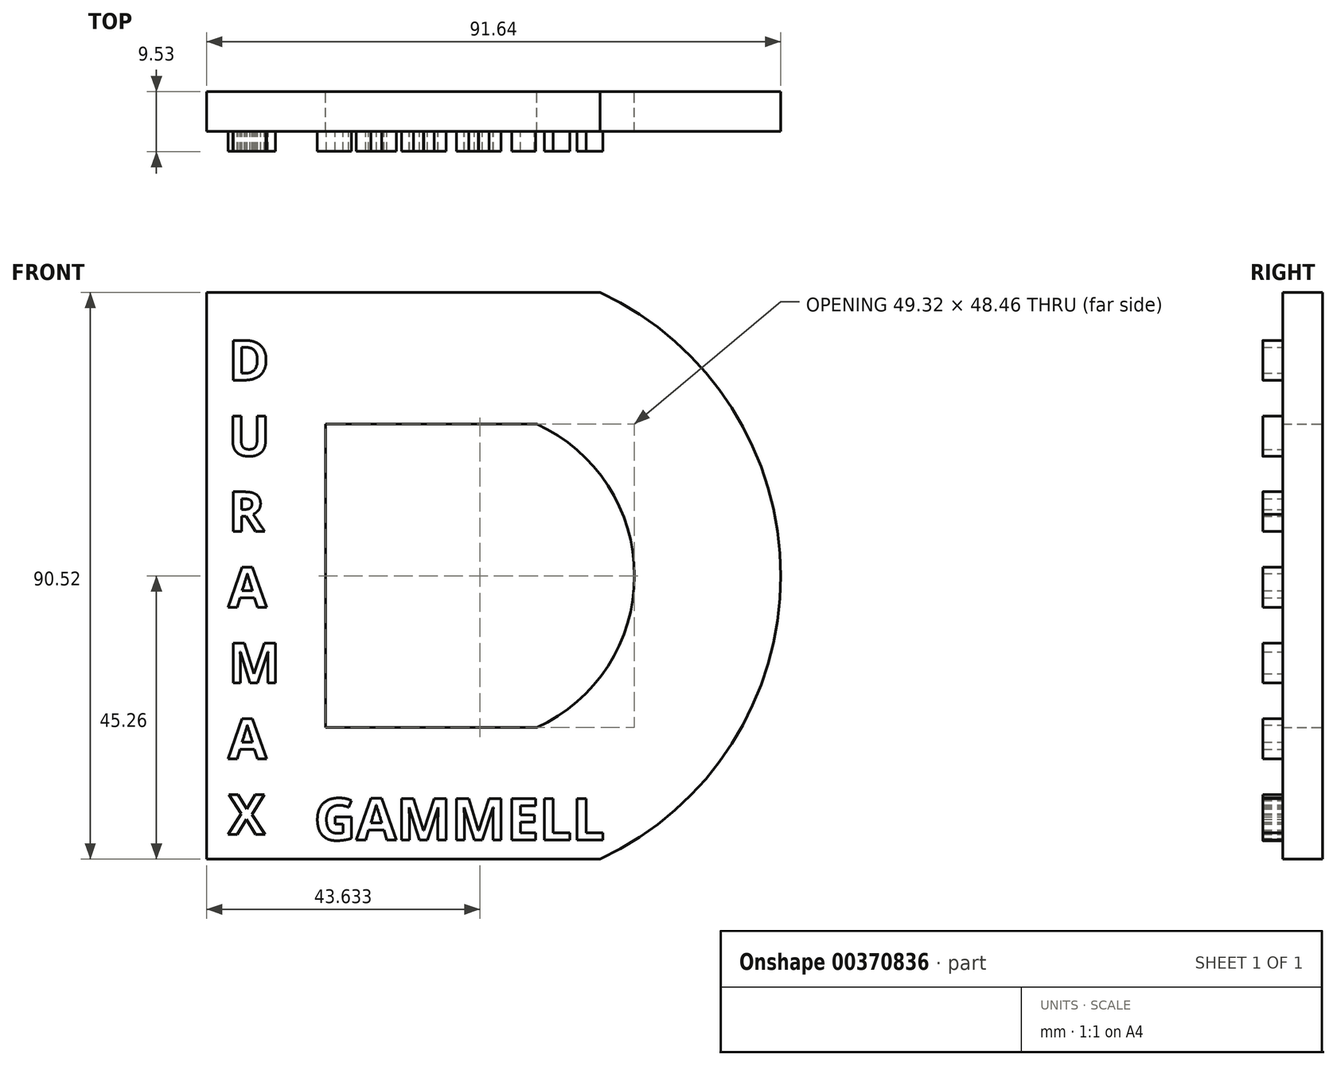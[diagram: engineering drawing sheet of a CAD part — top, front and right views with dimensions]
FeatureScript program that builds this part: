
annotation { "Feature Type Name" : "Feature", "Feature Type Description" : "" }
export const myFeature = defineFeature(function(context is Context, id is Id, definition is map)
    precondition{}
    {
        {
            var Q0;
            Q0=qCreatedBy(makeId("Front.planeOp"),FACE);
            var sketch = newSketch(context, id + "F0", { "sketchPlane" : qUnion([Q0])});
            skLineSegment(sketch, "E0.bottom", {"start": v(-41.68, 45.26) * mm, "end": v(21.14, 45.26) * mm});
            skLineSegment(sketch, "E0.top", {"start": v(-41.68, -45.26) * mm, "end": v(21.14, -45.26) * mm});
            skLineSegment(sketch, "E0.left", {"start": v(-41.68, 45.26) * mm, "end": v(-41.68, -45.26) * mm});
            skPoint(sketch, "E0.middle", {"position": v(0, 0) * mm});
            skLineSegment(sketch, "E1.top", {"start": v(-22.7, 24.23) * mm, "end": v(11, 24.23) * mm});
            skLineSegment(sketch, "E1.left", {"start": v(-22.7, -24.23) * mm, "end": v(-22.7, 24.23) * mm});
            skPoint(sketch, "E2.orphan", {"position": v(41.68, 45.26) * mm});
            skPoint(sketch, "E3.orphan", {"position": v(41.68, -45.26) * mm});
            skArc(sketch, "E4.trimOffspring", {"start": v(21.14, -45.26) * mm, "mid": v(49.96, 0) * mm, "end": v(21.14, 45.26) * mm});
            skPoint(sketch, "E5.orphan", {"position": v(22.7, 24.23) * mm});
            skPoint(sketch, "E6.orphan", {"position": v(22.7, -24.23) * mm});
            skLineSegment(sketch, "E7", {"start": v(-22.7, -24.23) * mm, "end": v(11, -24.23) * mm});
            skPoint(sketch, "E8.center.orphan", {"position": v(6.99, 0) * mm});
            skArc(sketch, "E9", {"start": v(11, -24.23) * mm, "mid": v(26.61, 0) * mm, "end": v(11, 24.23) * mm});
            skSolve(sketch);
        }
        {
            var Q0;
            Q0 = qSketchRegion(id + "F0", true);
            extrude(context, id + "F1", {"entities" : qUnion([Q0]), "depth" : 6.35 * mm});
        }
        {
            var Q0;
            Q0=makeQuery(id+"F0.imprint","IMPRINT",FACE,{"disambiguationData":[TD([[makeQuery(id+"F0.imprint","IMPRINT",EDGE,{"derivedFrom":sQuery(id+"F0.wireOp",EDGE,"E0.bottom")}),-1.0]])]});
            extrude(context, id + "F2", {"entities" : qUnion([Q0]), "operationType" : NewBodyOperationType.ADD, "depth" : 3.17 * mm});
        }
        {
            var Q0;
            Q0=makeQuery(id+"F1.opExtrude","CAP_FACE",FACE,{"disambiguationData":[OSD([sQuery(id+"F0.wireOp",EDGE,"E0.bottom"),sQuery(id+"F0.wireOp",EDGE,"E0.top"),sQuery(id+"F0.wireOp",EDGE,"E0.left"),sQuery(id+"F0.wireOp",EDGE,"E1.top"),sQuery(id+"F0.wireOp",EDGE,"E1.left"),sQuery(id+"F0.wireOp",EDGE,"E4.trimOffspring"),sQuery(id+"F0.wireOp",EDGE,"E7"),sQuery(id+"F0.wireOp",EDGE,"E9"),sQuery(id+"F0.wireOp",EDGE,"4330573b-99e2-4243-b304-8aef4ccaa376.sketch_text.stroke-0"),sQuery(id+"F0.wireOp",EDGE,"4330573b-99e2-4243-b304-8aef4ccaa376.sketch_text.stroke-1"),sQuery(id+"F0.wireOp",EDGE,"4330573b-99e2-4243-b304-8aef4ccaa376.sketch_text.stroke-2"),sQuery(id+"F0.wireOp",EDGE,"4330573b-99e2-4243-b304-8aef4ccaa376.sketch_text.stroke-3"),sQuery(id+"F0.wireOp",EDGE,"4330573b-99e2-4243-b304-8aef4ccaa376.sketch_text.stroke-4"),sQuery(id+"F0.wireOp",EDGE,"4330573b-99e2-4243-b304-8aef4ccaa376.sketch_text.stroke-5"),sQuery(id+"F0.wireOp",EDGE,"4330573b-99e2-4243-b304-8aef4ccaa376.sketch_text.stroke-6"),sQuery(id+"F0.wireOp",EDGE,"4330573b-99e2-4243-b304-8aef4ccaa376.sketch_text.stroke-12"),sQuery(id+"F0.wireOp",EDGE,"4330573b-99e2-4243-b304-8aef4ccaa376.sketch_text.stroke-13"),sQuery(id+"F0.wireOp",EDGE,"4330573b-99e2-4243-b304-8aef4ccaa376.sketch_text.stroke-14"),sQuery(id+"F0.wireOp",EDGE,"4330573b-99e2-4243-b304-8aef4ccaa376.sketch_text.stroke-15"),sQuery(id+"F0.wireOp",EDGE,"4330573b-99e2-4243-b304-8aef4ccaa376.sketch_text.stroke-16"),sQuery(id+"F0.wireOp",EDGE,"4330573b-99e2-4243-b304-8aef4ccaa376.sketch_text.stroke-17"),sQuery(id+"F0.wireOp",EDGE,"4330573b-99e2-4243-b304-8aef4ccaa376.sketch_text.stroke-18"),sQuery(id+"F0.wireOp",EDGE,"4330573b-99e2-4243-b304-8aef4ccaa376.sketch_text.stroke-19"),sQuery(id+"F0.wireOp",EDGE,"4330573b-99e2-4243-b304-8aef4ccaa376.sketch_text.stroke-20"),sQuery(id+"F0.wireOp",EDGE,"4330573b-99e2-4243-b304-8aef4ccaa376.sketch_text.stroke-21"),sQuery(id+"F0.wireOp",EDGE,"4330573b-99e2-4243-b304-8aef4ccaa376.sketch_text.stroke-22"),sQuery(id+"F0.wireOp",EDGE,"4330573b-99e2-4243-b304-8aef4ccaa376.sketch_text.stroke-23"),sQuery(id+"F0.wireOp",EDGE,"4330573b-99e2-4243-b304-8aef4ccaa376.sketch_text.stroke-24"),sQuery(id+"F0.wireOp",EDGE,"4330573b-99e2-4243-b304-8aef4ccaa376.sketch_text.stroke-25"),sQuery(id+"F0.wireOp",EDGE,"4330573b-99e2-4243-b304-8aef4ccaa376.sketch_text.stroke-26"),sQuery(id+"F0.wireOp",EDGE,"4330573b-99e2-4243-b304-8aef4ccaa376.sketch_text.stroke-34"),sQuery(id+"F0.wireOp",EDGE,"4330573b-99e2-4243-b304-8aef4ccaa376.sketch_text.stroke-35"),sQuery(id+"F0.wireOp",EDGE,"4330573b-99e2-4243-b304-8aef4ccaa376.sketch_text.stroke-36"),sQuery(id+"F0.wireOp",EDGE,"4330573b-99e2-4243-b304-8aef4ccaa376.sketch_text.stroke-37"),sQuery(id+"F0.wireOp",EDGE,"4330573b-99e2-4243-b304-8aef4ccaa376.sketch_text.stroke-38"),sQuery(id+"F0.wireOp",EDGE,"4330573b-99e2-4243-b304-8aef4ccaa376.sketch_text.stroke-39"),sQuery(id+"F0.wireOp",EDGE,"4330573b-99e2-4243-b304-8aef4ccaa376.sketch_text.stroke-40"),sQuery(id+"F0.wireOp",EDGE,"4330573b-99e2-4243-b304-8aef4ccaa376.sketch_text.stroke-41"),sQuery(id+"F0.wireOp",EDGE,"4330573b-99e2-4243-b304-8aef4ccaa376.sketch_text.stroke-42"),sQuery(id+"F0.wireOp",EDGE,"4330573b-99e2-4243-b304-8aef4ccaa376.sketch_text.stroke-43"),sQuery(id+"F0.wireOp",EDGE,"4330573b-99e2-4243-b304-8aef4ccaa376.sketch_text.stroke-44"),sQuery(id+"F0.wireOp",EDGE,"4330573b-99e2-4243-b304-8aef4ccaa376.sketch_text.stroke-45"),sQuery(id+"F0.wireOp",EDGE,"4330573b-99e2-4243-b304-8aef4ccaa376.sketch_text.stroke-46"),sQuery(id+"F0.wireOp",EDGE,"4330573b-99e2-4243-b304-8aef4ccaa376.sketch_text.stroke-47"),sQuery(id+"F0.wireOp",EDGE,"4330573b-99e2-4243-b304-8aef4ccaa376.sketch_text.stroke-48"),sQuery(id+"F0.wireOp",EDGE,"4330573b-99e2-4243-b304-8aef4ccaa376.sketch_text.stroke-49"),sQuery(id+"F0.wireOp",EDGE,"4330573b-99e2-4243-b304-8aef4ccaa376.sketch_text.stroke-50"),sQuery(id+"F0.wireOp",EDGE,"4330573b-99e2-4243-b304-8aef4ccaa376.sketch_text.stroke-51"),sQuery(id+"F0.wireOp",EDGE,"4330573b-99e2-4243-b304-8aef4ccaa376.sketch_text.stroke-52"),sQuery(id+"F0.wireOp",EDGE,"4330573b-99e2-4243-b304-8aef4ccaa376.sketch_text.stroke-53"),sQuery(id+"F0.wireOp",EDGE,"4330573b-99e2-4243-b304-8aef4ccaa376.sketch_text.stroke-58"),sQuery(id+"F0.wireOp",EDGE,"4330573b-99e2-4243-b304-8aef4ccaa376.sketch_text.stroke-59"),sQuery(id+"F0.wireOp",EDGE,"4330573b-99e2-4243-b304-8aef4ccaa376.sketch_text.stroke-60"),sQuery(id+"F0.wireOp",EDGE,"4330573b-99e2-4243-b304-8aef4ccaa376.sketch_text.stroke-61"),sQuery(id+"F0.wireOp",EDGE,"4330573b-99e2-4243-b304-8aef4ccaa376.sketch_text.stroke-62"),sQuery(id+"F0.wireOp",EDGE,"4330573b-99e2-4243-b304-8aef4ccaa376.sketch_text.stroke-63"),sQuery(id+"F0.wireOp",EDGE,"4330573b-99e2-4243-b304-8aef4ccaa376.sketch_text.stroke-64"),sQuery(id+"F0.wireOp",EDGE,"4330573b-99e2-4243-b304-8aef4ccaa376.sketch_text.stroke-65"),sQuery(id+"F0.wireOp",EDGE,"4330573b-99e2-4243-b304-8aef4ccaa376.sketch_text.stroke-66"),sQuery(id+"F0.wireOp",EDGE,"4330573b-99e2-4243-b304-8aef4ccaa376.sketch_text.stroke-67"),sQuery(id+"F0.wireOp",EDGE,"4330573b-99e2-4243-b304-8aef4ccaa376.sketch_text.stroke-68"),sQuery(id+"F0.wireOp",EDGE,"4330573b-99e2-4243-b304-8aef4ccaa376.sketch_text.stroke-69"),sQuery(id+"F0.wireOp",EDGE,"4330573b-99e2-4243-b304-8aef4ccaa376.sketch_text.stroke-70"),sQuery(id+"F0.wireOp",EDGE,"4330573b-99e2-4243-b304-8aef4ccaa376.sketch_text.stroke-71"),sQuery(id+"F0.wireOp",EDGE,"4330573b-99e2-4243-b304-8aef4ccaa376.sketch_text.stroke-72"),sQuery(id+"F0.wireOp",EDGE,"4330573b-99e2-4243-b304-8aef4ccaa376.sketch_text.stroke-73"),sQuery(id+"F0.wireOp",EDGE,"4330573b-99e2-4243-b304-8aef4ccaa376.sketch_text.stroke-74"),sQuery(id+"F0.wireOp",EDGE,"4330573b-99e2-4243-b304-8aef4ccaa376.sketch_text.stroke-75"),sQuery(id+"F0.wireOp",EDGE,"4330573b-99e2-4243-b304-8aef4ccaa376.sketch_text.stroke-76"),sQuery(id+"F0.wireOp",EDGE,"4330573b-99e2-4243-b304-8aef4ccaa376.sketch_text.stroke-77"),sQuery(id+"F0.wireOp",EDGE,"4330573b-99e2-4243-b304-8aef4ccaa376.sketch_text.stroke-78"),sQuery(id+"F0.wireOp",EDGE,"4330573b-99e2-4243-b304-8aef4ccaa376.sketch_text.stroke-79"),sQuery(id+"F0.wireOp",EDGE,"4330573b-99e2-4243-b304-8aef4ccaa376.sketch_text.stroke-80"),sQuery(id+"F0.wireOp",EDGE,"4330573b-99e2-4243-b304-8aef4ccaa376.sketch_text.stroke-81"),sQuery(id+"F0.wireOp",EDGE,"4330573b-99e2-4243-b304-8aef4ccaa376.sketch_text.stroke-82"),sQuery(id+"F0.wireOp",EDGE,"4330573b-99e2-4243-b304-8aef4ccaa376.sketch_text.stroke-83"),sQuery(id+"F0.wireOp",EDGE,"4330573b-99e2-4243-b304-8aef4ccaa376.sketch_text.stroke-84"),sQuery(id+"F0.wireOp",EDGE,"4330573b-99e2-4243-b304-8aef4ccaa376.sketch_text.stroke-89"),sQuery(id+"F0.wireOp",EDGE,"4330573b-99e2-4243-b304-8aef4ccaa376.sketch_text.stroke-90"),sQuery(id+"F0.wireOp",EDGE,"4330573b-99e2-4243-b304-8aef4ccaa376.sketch_text.stroke-91"),sQuery(id+"F0.wireOp",EDGE,"4330573b-99e2-4243-b304-8aef4ccaa376.sketch_text.stroke-92"),sQuery(id+"F0.wireOp",EDGE,"4330573b-99e2-4243-b304-8aef4ccaa376.sketch_text.stroke-93"),sQuery(id+"F0.wireOp",EDGE,"4330573b-99e2-4243-b304-8aef4ccaa376.sketch_text.stroke-94"),sQuery(id+"F0.wireOp",EDGE,"4330573b-99e2-4243-b304-8aef4ccaa376.sketch_text.stroke-95"),sQuery(id+"F0.wireOp",EDGE,"4330573b-99e2-4243-b304-8aef4ccaa376.sketch_text.stroke-96"),sQuery(id+"F0.wireOp",EDGE,"4330573b-99e2-4243-b304-8aef4ccaa376.sketch_text.stroke-97"),sQuery(id+"F0.wireOp",EDGE,"4330573b-99e2-4243-b304-8aef4ccaa376.sketch_text.stroke-98"),sQuery(id+"F0.wireOp",EDGE,"4330573b-99e2-4243-b304-8aef4ccaa376.sketch_text.stroke-99"),sQuery(id+"F0.wireOp",EDGE,"4330573b-99e2-4243-b304-8aef4ccaa376.sketch_text.stroke-100"),sQuery(id+"F0.wireOp",EDGE,"e53d3f8c-f9ea-4462-868c-9bd13cdbc47c.sketch_text.stroke-0"),sQuery(id+"F0.wireOp",EDGE,"e53d3f8c-f9ea-4462-868c-9bd13cdbc47c.sketch_text.stroke-1"),sQuery(id+"F0.wireOp",EDGE,"e53d3f8c-f9ea-4462-868c-9bd13cdbc47c.sketch_text.stroke-2"),sQuery(id+"F0.wireOp",EDGE,"e53d3f8c-f9ea-4462-868c-9bd13cdbc47c.sketch_text.stroke-3"),sQuery(id+"F0.wireOp",EDGE,"e53d3f8c-f9ea-4462-868c-9bd13cdbc47c.sketch_text.stroke-4"),sQuery(id+"F0.wireOp",EDGE,"e53d3f8c-f9ea-4462-868c-9bd13cdbc47c.sketch_text.stroke-5"),sQuery(id+"F0.wireOp",EDGE,"e53d3f8c-f9ea-4462-868c-9bd13cdbc47c.sketch_text.stroke-6"),sQuery(id+"F0.wireOp",EDGE,"e53d3f8c-f9ea-4462-868c-9bd13cdbc47c.sketch_text.stroke-7"),sQuery(id+"F0.wireOp",EDGE,"e53d3f8c-f9ea-4462-868c-9bd13cdbc47c.sketch_text.stroke-8"),sQuery(id+"F0.wireOp",EDGE,"e53d3f8c-f9ea-4462-868c-9bd13cdbc47c.sketch_text.stroke-9"),sQuery(id+"F0.wireOp",EDGE,"e53d3f8c-f9ea-4462-868c-9bd13cdbc47c.sketch_text.stroke-10"),sQuery(id+"F0.wireOp",EDGE,"e53d3f8c-f9ea-4462-868c-9bd13cdbc47c.sketch_text.stroke-11"),sQuery(id+"F0.wireOp",EDGE,"e53d3f8c-f9ea-4462-868c-9bd13cdbc47c.sketch_text.stroke-12"),sQuery(id+"F0.wireOp",EDGE,"e53d3f8c-f9ea-4462-868c-9bd13cdbc47c.sketch_text.stroke-13"),sQuery(id+"F0.wireOp",EDGE,"e53d3f8c-f9ea-4462-868c-9bd13cdbc47c.sketch_text.stroke-14"),sQuery(id+"F0.wireOp",EDGE,"e53d3f8c-f9ea-4462-868c-9bd13cdbc47c.sketch_text.stroke-15"),sQuery(id+"F0.wireOp",EDGE,"e53d3f8c-f9ea-4462-868c-9bd13cdbc47c.sketch_text.stroke-16"),sQuery(id+"F0.wireOp",EDGE,"e53d3f8c-f9ea-4462-868c-9bd13cdbc47c.sketch_text.stroke-17"),sQuery(id+"F0.wireOp",EDGE,"e53d3f8c-f9ea-4462-868c-9bd13cdbc47c.sketch_text.stroke-18"),sQuery(id+"F0.wireOp",EDGE,"e53d3f8c-f9ea-4462-868c-9bd13cdbc47c.sketch_text.stroke-19"),sQuery(id+"F0.wireOp",EDGE,"e53d3f8c-f9ea-4462-868c-9bd13cdbc47c.sketch_text.stroke-20"),sQuery(id+"F0.wireOp",EDGE,"e53d3f8c-f9ea-4462-868c-9bd13cdbc47c.sketch_text.stroke-21"),sQuery(id+"F0.wireOp",EDGE,"e53d3f8c-f9ea-4462-868c-9bd13cdbc47c.sketch_text.stroke-22"),sQuery(id+"F0.wireOp",EDGE,"e53d3f8c-f9ea-4462-868c-9bd13cdbc47c.sketch_text.stroke-23"),sQuery(id+"F0.wireOp",EDGE,"e53d3f8c-f9ea-4462-868c-9bd13cdbc47c.sketch_text.stroke-24"),sQuery(id+"F0.wireOp",EDGE,"e53d3f8c-f9ea-4462-868c-9bd13cdbc47c.sketch_text.stroke-25"),sQuery(id+"F0.wireOp",EDGE,"e53d3f8c-f9ea-4462-868c-9bd13cdbc47c.sketch_text.stroke-26"),sQuery(id+"F0.wireOp",EDGE,"e53d3f8c-f9ea-4462-868c-9bd13cdbc47c.sketch_text.stroke-31"),sQuery(id+"F0.wireOp",EDGE,"e53d3f8c-f9ea-4462-868c-9bd13cdbc47c.sketch_text.stroke-32"),sQuery(id+"F0.wireOp",EDGE,"e53d3f8c-f9ea-4462-868c-9bd13cdbc47c.sketch_text.stroke-33"),sQuery(id+"F0.wireOp",EDGE,"e53d3f8c-f9ea-4462-868c-9bd13cdbc47c.sketch_text.stroke-34"),sQuery(id+"F0.wireOp",EDGE,"e53d3f8c-f9ea-4462-868c-9bd13cdbc47c.sketch_text.stroke-35"),sQuery(id+"F0.wireOp",EDGE,"e53d3f8c-f9ea-4462-868c-9bd13cdbc47c.sketch_text.stroke-36"),sQuery(id+"F0.wireOp",EDGE,"e53d3f8c-f9ea-4462-868c-9bd13cdbc47c.sketch_text.stroke-37"),sQuery(id+"F0.wireOp",EDGE,"e53d3f8c-f9ea-4462-868c-9bd13cdbc47c.sketch_text.stroke-38"),sQuery(id+"F0.wireOp",EDGE,"e53d3f8c-f9ea-4462-868c-9bd13cdbc47c.sketch_text.stroke-39"),sQuery(id+"F0.wireOp",EDGE,"e53d3f8c-f9ea-4462-868c-9bd13cdbc47c.sketch_text.stroke-40"),sQuery(id+"F0.wireOp",EDGE,"e53d3f8c-f9ea-4462-868c-9bd13cdbc47c.sketch_text.stroke-41"),sQuery(id+"F0.wireOp",EDGE,"e53d3f8c-f9ea-4462-868c-9bd13cdbc47c.sketch_text.stroke-42"),sQuery(id+"F0.wireOp",EDGE,"e53d3f8c-f9ea-4462-868c-9bd13cdbc47c.sketch_text.stroke-43"),sQuery(id+"F0.wireOp",EDGE,"e53d3f8c-f9ea-4462-868c-9bd13cdbc47c.sketch_text.stroke-44"),sQuery(id+"F0.wireOp",EDGE,"e53d3f8c-f9ea-4462-868c-9bd13cdbc47c.sketch_text.stroke-45"),sQuery(id+"F0.wireOp",EDGE,"e53d3f8c-f9ea-4462-868c-9bd13cdbc47c.sketch_text.stroke-46"),sQuery(id+"F0.wireOp",EDGE,"e53d3f8c-f9ea-4462-868c-9bd13cdbc47c.sketch_text.stroke-47"),sQuery(id+"F0.wireOp",EDGE,"e53d3f8c-f9ea-4462-868c-9bd13cdbc47c.sketch_text.stroke-48"),sQuery(id+"F0.wireOp",EDGE,"e53d3f8c-f9ea-4462-868c-9bd13cdbc47c.sketch_text.stroke-49"),sQuery(id+"F0.wireOp",EDGE,"e53d3f8c-f9ea-4462-868c-9bd13cdbc47c.sketch_text.stroke-50"),sQuery(id+"F0.wireOp",EDGE,"e53d3f8c-f9ea-4462-868c-9bd13cdbc47c.sketch_text.stroke-51"),sQuery(id+"F0.wireOp",EDGE,"e53d3f8c-f9ea-4462-868c-9bd13cdbc47c.sketch_text.stroke-52"),sQuery(id+"F0.wireOp",EDGE,"e53d3f8c-f9ea-4462-868c-9bd13cdbc47c.sketch_text.stroke-53"),sQuery(id+"F0.wireOp",EDGE,"e53d3f8c-f9ea-4462-868c-9bd13cdbc47c.sketch_text.stroke-54"),sQuery(id+"F0.wireOp",EDGE,"e53d3f8c-f9ea-4462-868c-9bd13cdbc47c.sketch_text.stroke-55"),sQuery(id+"F0.wireOp",EDGE,"e53d3f8c-f9ea-4462-868c-9bd13cdbc47c.sketch_text.stroke-56"),sQuery(id+"F0.wireOp",EDGE,"e53d3f8c-f9ea-4462-868c-9bd13cdbc47c.sketch_text.stroke-57"),sQuery(id+"F0.wireOp",EDGE,"e53d3f8c-f9ea-4462-868c-9bd13cdbc47c.sketch_text.stroke-58"),sQuery(id+"F0.wireOp",EDGE,"e53d3f8c-f9ea-4462-868c-9bd13cdbc47c.sketch_text.stroke-59"),sQuery(id+"F0.wireOp",EDGE,"e53d3f8c-f9ea-4462-868c-9bd13cdbc47c.sketch_text.stroke-60"),sQuery(id+"F0.wireOp",EDGE,"e53d3f8c-f9ea-4462-868c-9bd13cdbc47c.sketch_text.stroke-61"),sQuery(id+"F0.wireOp",EDGE,"e53d3f8c-f9ea-4462-868c-9bd13cdbc47c.sketch_text.stroke-62"),sQuery(id+"F0.wireOp",EDGE,"e53d3f8c-f9ea-4462-868c-9bd13cdbc47c.sketch_text.stroke-63"),sQuery(id+"F0.wireOp",EDGE,"e53d3f8c-f9ea-4462-868c-9bd13cdbc47c.sketch_text.stroke-64"),sQuery(id+"F0.wireOp",EDGE,"e53d3f8c-f9ea-4462-868c-9bd13cdbc47c.sketch_text.stroke-65"),sQuery(id+"F0.wireOp",EDGE,"e53d3f8c-f9ea-4462-868c-9bd13cdbc47c.sketch_text.stroke-66"),sQuery(id+"F0.wireOp",EDGE,"e53d3f8c-f9ea-4462-868c-9bd13cdbc47c.sketch_text.stroke-67"),sQuery(id+"F0.wireOp",EDGE,"e53d3f8c-f9ea-4462-868c-9bd13cdbc47c.sketch_text.stroke-68"),sQuery(id+"F0.wireOp",EDGE,"e53d3f8c-f9ea-4462-868c-9bd13cdbc47c.sketch_text.stroke-69"),sQuery(id+"F0.wireOp",EDGE,"e53d3f8c-f9ea-4462-868c-9bd13cdbc47c.sketch_text.stroke-70"),sQuery(id+"F0.wireOp",EDGE,"e53d3f8c-f9ea-4462-868c-9bd13cdbc47c.sketch_text.stroke-71"),sQuery(id+"F0.wireOp",EDGE,"e53d3f8c-f9ea-4462-868c-9bd13cdbc47c.sketch_text.stroke-72"),sQuery(id+"F0.wireOp",EDGE,"e53d3f8c-f9ea-4462-868c-9bd13cdbc47c.sketch_text.stroke-73"),sQuery(id+"F0.wireOp",EDGE,"e53d3f8c-f9ea-4462-868c-9bd13cdbc47c.sketch_text.stroke-74"),sQuery(id+"F0.wireOp",EDGE,"e53d3f8c-f9ea-4462-868c-9bd13cdbc47c.sketch_text.stroke-75"),sQuery(id+"F0.wireOp",EDGE,"e53d3f8c-f9ea-4462-868c-9bd13cdbc47c.sketch_text.stroke-76"),sQuery(id+"F0.wireOp",EDGE,"e53d3f8c-f9ea-4462-868c-9bd13cdbc47c.sketch_text.stroke-77"),sQuery(id+"F0.wireOp",EDGE,"e53d3f8c-f9ea-4462-868c-9bd13cdbc47c.sketch_text.stroke-78"),sQuery(id+"F0.wireOp",EDGE,"e53d3f8c-f9ea-4462-868c-9bd13cdbc47c.sketch_text.stroke-79"),sQuery(id+"F0.wireOp",EDGE,"e53d3f8c-f9ea-4462-868c-9bd13cdbc47c.sketch_text.stroke-80"),sQuery(id+"F0.wireOp",EDGE,"e53d3f8c-f9ea-4462-868c-9bd13cdbc47c.sketch_text.stroke-81"),sQuery(id+"F0.wireOp",EDGE,"e53d3f8c-f9ea-4462-868c-9bd13cdbc47c.sketch_text.stroke-82"),sQuery(id+"F0.wireOp",EDGE,"e53d3f8c-f9ea-4462-868c-9bd13cdbc47c.sketch_text.stroke-83"),sQuery(id+"F0.wireOp",EDGE,"e53d3f8c-f9ea-4462-868c-9bd13cdbc47c.sketch_text.stroke-84"),sQuery(id+"F0.wireOp",EDGE,"e53d3f8c-f9ea-4462-868c-9bd13cdbc47c.sketch_text.stroke-85"),sQuery(id+"F0.wireOp",EDGE,"e53d3f8c-f9ea-4462-868c-9bd13cdbc47c.sketch_text.stroke-86"),sQuery(id+"F0.wireOp",EDGE,"e53d3f8c-f9ea-4462-868c-9bd13cdbc47c.sketch_text.stroke-87"),sQuery(id+"F0.wireOp",EDGE,"e53d3f8c-f9ea-4462-868c-9bd13cdbc47c.sketch_text.stroke-88"),sQuery(id+"F0.wireOp",EDGE,"e53d3f8c-f9ea-4462-868c-9bd13cdbc47c.sketch_text.stroke-89"),sQuery(id+"F0.wireOp",EDGE,"e53d3f8c-f9ea-4462-868c-9bd13cdbc47c.sketch_text.stroke-90"),sQuery(id+"F0.wireOp",EDGE,"e53d3f8c-f9ea-4462-868c-9bd13cdbc47c.sketch_text.stroke-91"),sQuery(id+"F0.wireOp",EDGE,"e53d3f8c-f9ea-4462-868c-9bd13cdbc47c.sketch_text.stroke-92")])],"isStart":false});
            var sketch = newSketch(context, id + "F3", { "sketchPlane" : qUnion([Q0])});
            skPoint(sketch, "E10.middle", {"position": v(0, 0) * mm});
            skPoint(sketch, "E11.orphan", {"position": v(41.68, 45.26) * mm});
            skPoint(sketch, "E12.orphan", {"position": v(41.68, -45.26) * mm});
            skPoint(sketch, "E13.orphan", {"position": v(22.7, 24.23) * mm});
            skPoint(sketch, "E14.orphan", {"position": v(22.7, -24.23) * mm});
            skPoint(sketch, "E15.center.orphan", {"position": v(6.99, 0) * mm});
            skText(sketch, "E16", { "text": "D\nU\nR\nA\nM\nA\nX", "fontName": "OpenSans-Bold.ttf"});
            skText(sketch, "E17", { "text": "GAMMELL", "fontName": "OpenSans-Bold.ttf"});
            skPoint(sketch, "E10.left.start.orphan", {"position": v(-41.68, 45.26) * mm});
            skPoint(sketch, "E10.top.start.orphan", {"position": v(-41.68, -45.26) * mm});
            const initialGuessF3  = {"E16": [-0.03825, 0.03124, 1, 0, 0.0064], "E17": [-0.02454, -0.04221, 1, 0, 0.0067]};
            skSetInitialGuess(sketch, initialGuessF3);
            skSolve(sketch);
        }
        {
            var Q0;
            Q0 = qSketchRegion(id + "F3", true);
            extrude(context, id + "F4", {"entities" : qUnion([Q0]), "operationType" : NewBodyOperationType.ADD, "depth" : 3.17 * mm});
        }
    });
